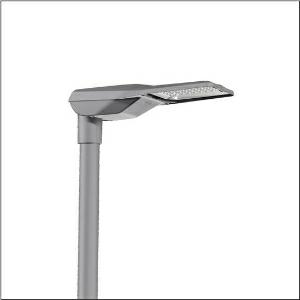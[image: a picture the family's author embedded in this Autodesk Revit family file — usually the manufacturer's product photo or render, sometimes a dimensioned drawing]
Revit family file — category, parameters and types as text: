
# Revit family: streetlight_sl_21_iq_mini___pl52_5xe2h31d08hb_f62b
name_source: partatom
category: Lighting Fixtures
units: mm (PartAtom-declared; Revit-internal decimal feet)

## family parameters
Cut with Voids When Loaded = No
Host = Face
Light Source = No
Part Type = Normal
Room Calculation Point = No
Round Connector Dimension = Use Diameter
Shared = No

## types (1)
- --- (1 x LED, 9290 lm, 70.9 W, 3000K)
    Apparent Load = 71 VA
    CIE Flux Codes = 27 59 98 100 100
    Color Rendering = 70
    Color Temperature = 3000K
    Default Elevation = 1800 mm
    Description = Streetlight SL 21 mini, mast luminaire, primary light control with lens, of PMMA, primary optical cover: cover, of toughened safety glass, transparent, light distribution: PL52, light emission: direct distribution, primary light characteristic: asymmetric, installation type: post-top, side-entry, LED, High Power LED, rated luminous flux: 9.290lm, luminous efficacy: 131lm/W, light colour: 730, colour temperature: 3000K, control gear: ECG iQ, control: Auto-Match, Temp-Guard, Lumen-Switch, Night-Set, Smart-Wire, Light-Fading, Desk-Remote (wireless, voltage-free reading and setting of iQ features in the workshop via application-optimized NFC function/RFID function), optimised constant luminous flux control (CLO 2.0), mains connection: 220..240V, AC, 50/60Hz, start of lifetime: 71W, end of lifetime: 75W, reduction: 31W, luminaire housing, of diecast aluminium, powder-coated, Siteco® metallic grey (DB 702S), corrosivity category C5 according to DIN EN ISO 12944, length: 628mm, width: 235mm, height: 110mm, spigot size: 60/76mm (post-top) and 42/60/76mm (side-entry), mast flange for spigot size: 42mm: 5XC10008XM4, 60mm: 5XC10008XM2, 76/60mm: 5XC10108XM1, protection rating (complete): IP66, insulation class (complete): insulation class II (safety insulation), certification: CE, ENEC, VDE, impact resistance: IK09, permissible operating ambient temperature for outdoor applications: -40..+50°C, standard-compliant lighting for roads and squares, packaging unit: 1 piece

Light Distribution: PL52
    Height = 110 mm
    Lamp = 1 x LED
    Lamp Light Flux = 9290 lm
    Lamp Power = 70.9 W
    Lamp count = 1
    Length = 625 mm
    Luminous efficacy = 131 lm/W
    Manufacturer = Siteco
    ModVariant = No
    Model = 5XE2H31D08HB
    Number of Poles = 1
    OnlyDefault = Yes
    Power Factor = 1
    Product Name = Streetlight SL 21 iQ mini | PL52
    Product group = mast luminaire | pylon top
    ProductGroupID = 6100
    Protection Class = Protection class II
    Protection Degree = IP 66
    RLX_Detail_Level = 1
    RlxData = <blob elided: 101881 chars, md5=01e11ab6>
    Socket = socket
    Standby Power = 0 W
    System Light Flux = 9290 lm
    System Power = 71 W
    Type Comments = factory setting: luminous flux: 100 % | dim-lin: 254 | 711 mA
    Type Image = l_1003519.jpg
    URL = http://relux.com
    VarID = @adj_069721
    Voltage = 0 V
    Weight = 0.00 kg
    Width = 234 mm

## geometry (parser evidence)
native form markers: Blend x4, Sweep x10
no freeform markers — native parametric forms only
